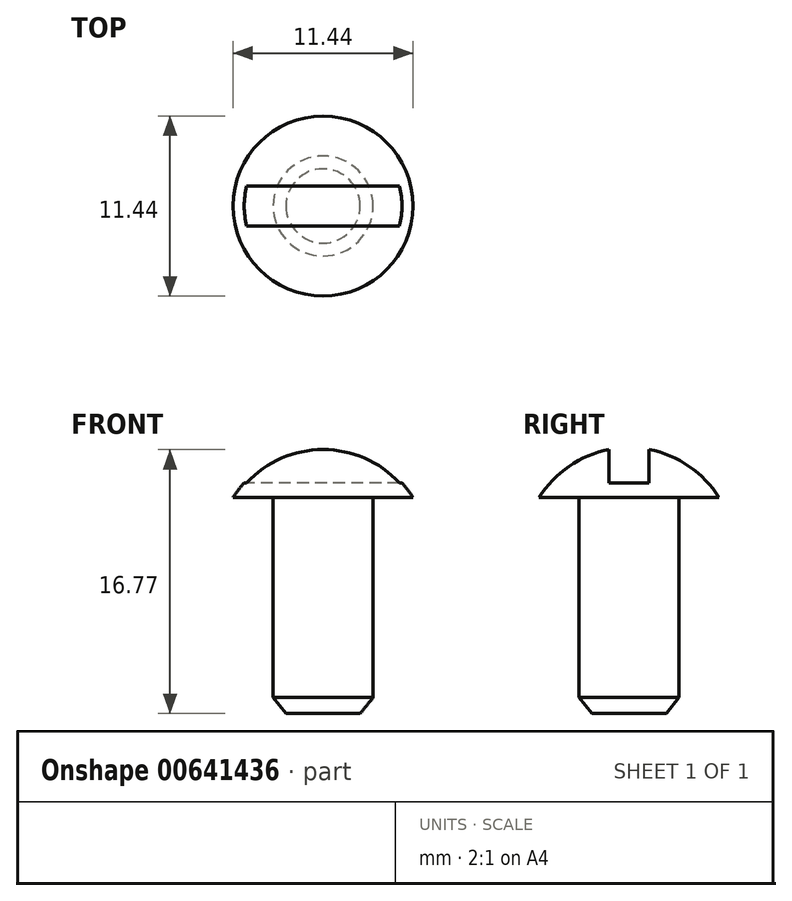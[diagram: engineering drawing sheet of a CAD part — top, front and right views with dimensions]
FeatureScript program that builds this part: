
annotation { "Feature Type Name" : "Feature", "Feature Type Description" : "" }
export const myFeature = defineFeature(function(context is Context, id is Id, definition is map)
    precondition{}
    {
        {
            var Q0;
            Q0=qCreatedBy(makeId("Front.planeOp"),FACE);
            var sketch = newSketch(context, id + "F0", { "sketchPlane" : qUnion([Q0])});
            skLineSegment(sketch, "E0", {"start": v(0, 6.73) * mm, "end": v(0, -9.14) * mm});
            skLineSegment(sketch, "E1", {"start": v(0, -9.14) * mm, "end": v(3.18, -9.14) * mm});
            skLineSegment(sketch, "E2", {"start": v(3.18, -9.14) * mm, "end": v(3.18, 3.56) * mm});
            skLineSegment(sketch, "E3", {"start": v(3.18, 3.56) * mm, "end": v(5.72, 3.56) * mm});
            skArc(sketch, "E4", {"start": v(5.72, 3.56) * mm, "mid": v(3.27, 5.88) * mm, "end": v(0, 6.73) * mm});
            skPoint(sketch, "E5.orphan", {"position": v(0, 7.94) * mm});
            skSolve(sketch);
        }
        {
            var Q0;
            Q0=makeQuery(id+"F0.imprint","IMPRINT",FACE,{"disambiguationData":[TD([[makeQuery(id+"F0.imprint","IMPRINT",EDGE,{"derivedFrom":sQuery(id+"F0.wireOp",EDGE,"E0")}),1.0]])]});
            var Q1;
            Q1=sQuery(id+"F0.wireOp",EDGE,"E0");
            revolve(context, id + "F1", {"entities" : qUnion([Q0]), "axis" : qUnion([Q1]), "revolveType" : RevolveType.FULL});
        }
        {
            var Q0;
            Q0=makeQuery(id+"F1.opRevolve","SWEPT_FACE",FACE,{"disambiguationData":[OSD([sQuery(id+"F0.wireOp",EDGE,"E1")])]});
            cPlane(context, id + "F2", {"entities" : qUnion([Q0]), "cplaneType" : CPlaneType.OFFSET, "offset" : 1.02 * mm, "width" : 152.4 * mm, "height" : 152.4 * mm});
        }
        {
            var Q0;
            Q0=qCreatedBy(id+"F2.planeOp",FACE);
            var sketch = newSketch(context, id + "F3", { "sketchPlane" : qUnion([Q0])});
            skCircle(sketch, "E6", {"center": v(0, 0) * mm, "radius": 2.36 * mm});
            skSolve(sketch);
        }
        {
            var Q1;
            Q1=makeQuery(id+"F1.opRevolve","SWEPT_FACE",FACE,{"disambiguationData":[OSD([sQuery(id+"F0.wireOp",EDGE,"E1")])]});
            var Q2;
            Q2=makeQuery(id+"F3.imprint","IMPRINT",FACE,{"disambiguationData":[TD([[makeQuery(id+"F3.imprint","IMPRINT",EDGE,{"derivedFrom":sQuery(id+"F3.wireOp",EDGE,"E6")}),1.0]])]});
            loft(context, id + "F4", {"operationType" : NewBodyOperationType.ADD, "sheetProfilesArray" : [{ "sheetProfileEntities" : qUnion([Q1]) }, { "sheetProfileEntities" : qUnion([Q2]) }]});
        }
        {
            var Q0;
            Q0=qCreatedBy(id+"F2.planeOp",FACE);
            cPlane(context, id + "F5", {"entities" : qUnion([Q0]), "cplaneType" : CPlaneType.OFFSET, "offset" : 17.04 * mm, "oppositeDirection" : true, "width" : 152.4 * mm, "height" : 152.4 * mm});
        }
        {
            var Q0;
            Q0=qCreatedBy(id+"F5.planeOp",FACE);
            var sketch = newSketch(context, id + "F6", { "sketchPlane" : qUnion([Q0])});
            skLineSegment(sketch, "E7.bottom", {"start": v(5.08, 1.27) * mm, "end": v(-5.08, 1.27) * mm});
            skLineSegment(sketch, "E7.top", {"start": v(5.08, -1.27) * mm, "end": v(-5.08, -1.27) * mm});
            skLineSegment(sketch, "E7.left", {"start": v(5.08, 1.27) * mm, "end": v(5.08, -1.27) * mm});
            skLineSegment(sketch, "E7.right", {"start": v(-5.08, 1.27) * mm, "end": v(-5.08, -1.27) * mm});
            skPoint(sketch, "E7.middle", {"position": v(0, 0) * mm});
            skSolve(sketch);
        }
        {
            var Q0;
            Q0=makeQuery(id+"F6.imprint","IMPRINT",FACE,{"disambiguationData":[TD([[makeQuery(id+"F6.imprint","IMPRINT",EDGE,{"derivedFrom":sQuery(id+"F6.wireOp",EDGE,"E7.bottom")}),1.0]])]});
            extrude(context, id + "F7", {"entities" : qUnion([Q0]), "operationType" : NewBodyOperationType.REMOVE, "depth" : 2.4 * mm, "offsetDistance" : 25.4 * mm});
        }
    });
